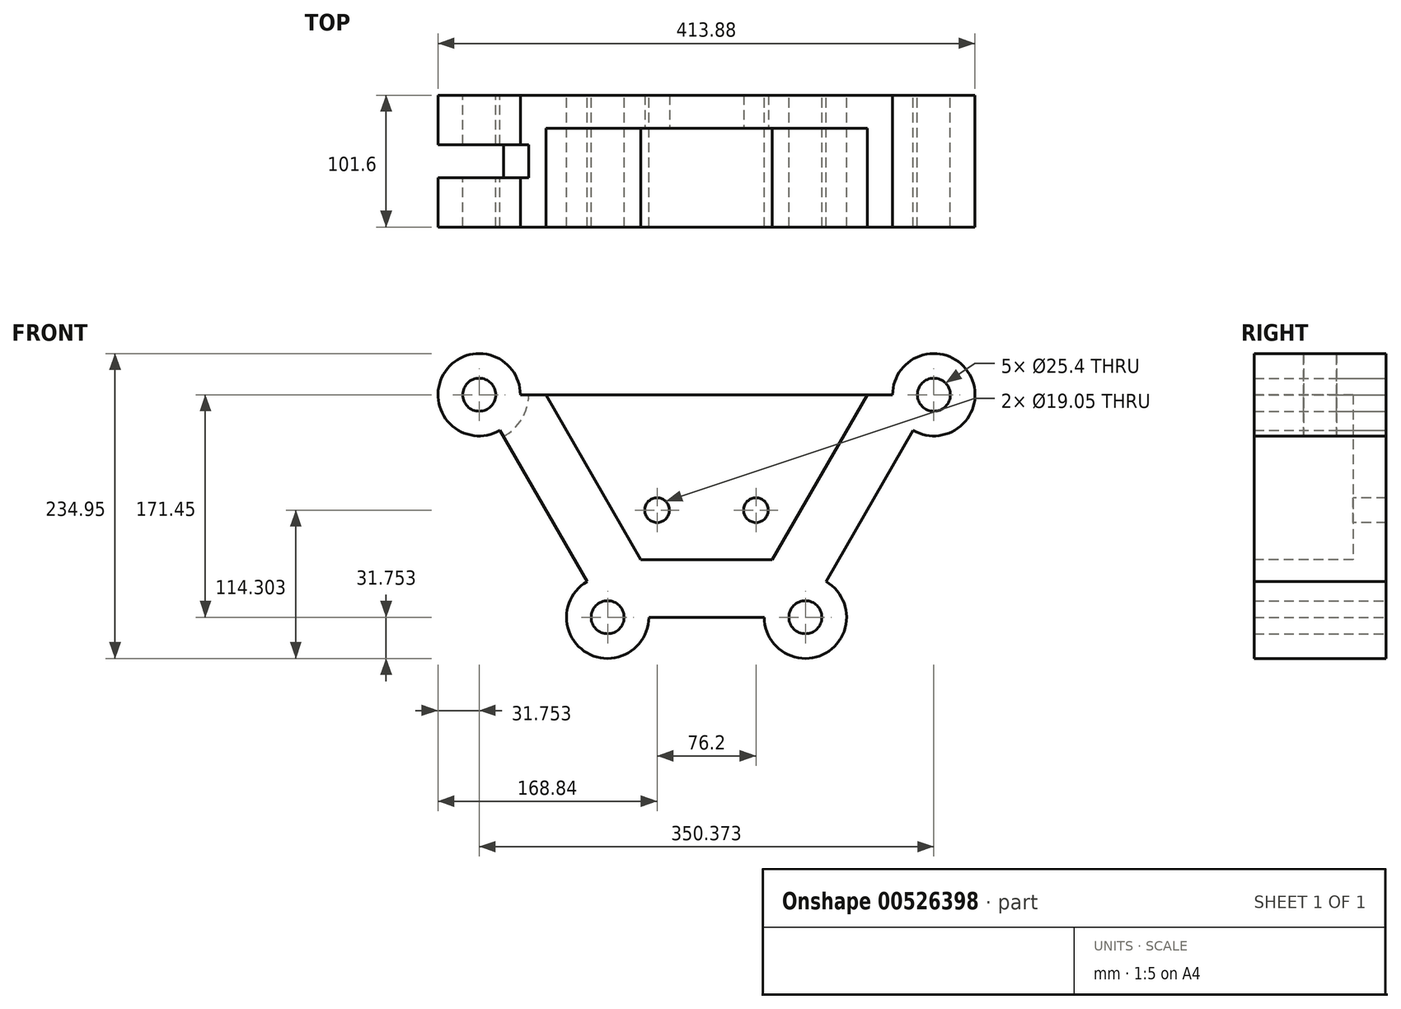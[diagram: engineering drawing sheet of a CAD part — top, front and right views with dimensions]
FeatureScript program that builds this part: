
annotation { "Feature Type Name" : "Feature", "Feature Type Description" : "" }
export const myFeature = defineFeature(function(context is Context, id is Id, definition is map)
    precondition{}
    {
        {
            var Q0;
            Q0=qCreatedBy(makeId("Front.planeOp"),FACE);
            var sketch = newSketch(context, id + "F0", { "sketchPlane" : qUnion([Q0])});
            skLineSegment(sketch, "E0", {"start": v(-76.2, -88.68) * mm, "end": v(76.2, -88.68) * mm});
            skLineSegment(sketch, "E1", {"start": v(-175.19, 82.77) * mm, "end": v(175.19, 82.77) * mm});
            skLineSegment(sketch, "E2", {"start": v(0, 82.77) * mm, "end": v(0, -88.68) * mm, "construction": true});
            skLineSegment(sketch, "E3", {"start": v(175.19, 82.77) * mm, "end": v(76.2, -88.68) * mm});
            skLineSegment(sketch, "E4", {"start": v(-175.19, 82.77) * mm, "end": v(-76.2, -88.68) * mm});
            skCircle(sketch, "E5", {"center": v(-175.19, 82.77) * mm, "radius": 31.75 * mm});
            skCircle(sketch, "E6", {"center": v(-175.19, 82.77) * mm, "radius": 12.7 * mm});
            skCircle(sketch, "E7", {"center": v(175.19, 82.77) * mm, "radius": 12.7 * mm});
            skCircle(sketch, "E8", {"center": v(76.2, -88.68) * mm, "radius": 12.7 * mm});
            skCircle(sketch, "E9", {"center": v(-76.2, -88.68) * mm, "radius": 12.7 * mm});
            skCircle(sketch, "E10", {"center": v(175.19, 82.77) * mm, "radius": 31.75 * mm});
            skCircle(sketch, "E11", {"center": v(76.2, -88.68) * mm, "radius": 31.75 * mm});
            skCircle(sketch, "E12", {"center": v(-76.2, -88.68) * mm, "radius": 31.75 * mm});
            skSolve(sketch);
        }
        {
            var Q0;
            {var subQ3=sQuery(id+"F0.wireOp",EDGE,"E12");var subQ10=sQuery(id+"F0.wireOp",EDGE,"E0");var subQ11=makeQuery(id+"F0.imprint","INTERSECT",VERTEX,{"derivedFrom":[subQ10,subQ3]});Q0=makeQuery(id+"F0.imprint","IMPRINT",FACE,{"disambiguationData":[TD([[makeQuery(id+"F0.imprint","IMPRINT",EDGE,{"disambiguationData":[TD([[subQ11,-1.0]])],"derivedFrom":subQ10}),1.0]])]});}
            var Q1;
            {var subQ0=sQuery(id+"F0.wireOp",EDGE,"E5");var subQ1=sQuery(id+"F0.wireOp",EDGE,"E1");var subQ2=makeQuery(id+"F0.imprint","INTERSECT",VERTEX,{"derivedFrom":[subQ1,subQ0]});Q1=makeQuery(id+"F0.imprint","IMPRINT",FACE,{"disambiguationData":[TD([[makeQuery(id+"F0.imprint","IMPRINT",EDGE,{"disambiguationData":[TD([[subQ2,1.0]])],"derivedFrom":subQ1}),-1.0]])]});}
            var Q2;
            {var subQ0=sQuery(id+"F0.wireOp",EDGE,"E5");var subQ1=sQuery(id+"F0.wireOp",EDGE,"E1");var subQ2=makeQuery(id+"F0.imprint","INTERSECT",VERTEX,{"derivedFrom":[subQ1,subQ0]});Q2=makeQuery(id+"F0.imprint","IMPRINT",FACE,{"disambiguationData":[TD([[makeQuery(id+"F0.imprint","IMPRINT",EDGE,{"disambiguationData":[TD([[subQ2,1.0]])],"derivedFrom":subQ1}),1.0]])]});}
            var Q3;
            {var subQ0=sQuery(id+"F0.wireOp",EDGE,"E10");var subQ1=sQuery(id+"F0.wireOp",EDGE,"E1");var subQ2=makeQuery(id+"F0.imprint","INTERSECT",VERTEX,{"derivedFrom":[subQ1,subQ0]});Q3=makeQuery(id+"F0.imprint","IMPRINT",FACE,{"disambiguationData":[TD([[makeQuery(id+"F0.imprint","IMPRINT",EDGE,{"disambiguationData":[TD([[subQ2,-1.0]])],"derivedFrom":subQ1}),1.0]])]});}
            var Q4;
            {var subQ0=sQuery(id+"F0.wireOp",EDGE,"E10");var subQ1=sQuery(id+"F0.wireOp",EDGE,"E1");var subQ2=makeQuery(id+"F0.imprint","INTERSECT",VERTEX,{"derivedFrom":[subQ1,subQ0]});Q4=makeQuery(id+"F0.imprint","IMPRINT",FACE,{"disambiguationData":[TD([[makeQuery(id+"F0.imprint","IMPRINT",EDGE,{"disambiguationData":[TD([[subQ2,-1.0]])],"derivedFrom":subQ1}),-1.0]])]});}
            var Q5;
            {var subQ0=sQuery(id+"F0.wireOp",EDGE,"E11");var subQ1=sQuery(id+"F0.wireOp",EDGE,"E0");var subQ2=makeQuery(id+"F0.imprint","INTERSECT",VERTEX,{"derivedFrom":[subQ1,subQ0]});Q5=makeQuery(id+"F0.imprint","IMPRINT",FACE,{"disambiguationData":[TD([[makeQuery(id+"F0.imprint","IMPRINT",EDGE,{"disambiguationData":[TD([[subQ2,-1.0]])],"derivedFrom":subQ1}),-1.0]])]});}
            var Q6;
            {var subQ0=sQuery(id+"F0.wireOp",EDGE,"E11");var subQ1=sQuery(id+"F0.wireOp",EDGE,"E0");var subQ2=makeQuery(id+"F0.imprint","INTERSECT",VERTEX,{"derivedFrom":[subQ1,subQ0]});Q6=makeQuery(id+"F0.imprint","IMPRINT",FACE,{"disambiguationData":[TD([[makeQuery(id+"F0.imprint","IMPRINT",EDGE,{"disambiguationData":[TD([[subQ2,-1.0]])],"derivedFrom":subQ1}),1.0]])]});}
            var Q7;
            {var subQ0=sQuery(id+"F0.wireOp",EDGE,"E12");var subQ1=sQuery(id+"F0.wireOp",EDGE,"E0");var subQ2=makeQuery(id+"F0.imprint","INTERSECT",VERTEX,{"derivedFrom":[subQ1,subQ0]});Q7=makeQuery(id+"F0.imprint","IMPRINT",FACE,{"disambiguationData":[TD([[makeQuery(id+"F0.imprint","IMPRINT",EDGE,{"disambiguationData":[TD([[subQ2,1.0]])],"derivedFrom":subQ1}),-1.0]])]});}
            var Q8;
            {var subQ0=sQuery(id+"F0.wireOp",EDGE,"E12");var subQ1=sQuery(id+"F0.wireOp",EDGE,"E0");var subQ2=makeQuery(id+"F0.imprint","INTERSECT",VERTEX,{"derivedFrom":[subQ1,subQ0]});Q8=makeQuery(id+"F0.imprint","IMPRINT",FACE,{"disambiguationData":[TD([[makeQuery(id+"F0.imprint","IMPRINT",EDGE,{"disambiguationData":[TD([[subQ2,1.0]])],"derivedFrom":subQ1}),1.0]])]});}
            extrude(context, id + "F1", {"entities" : qUnion([Q0, Q1, Q2, Q3, Q4, Q5, Q6, Q7, Q8]), "endBound" : BoundingType.SYMMETRIC, "depth" : 101.6 * mm, "offsetDistance" : 25.4 * mm});
        }
        {
            var Q0;
            Q0=makeQuery(id+"F1.opExtrude","CAP_FACE",FACE,{"disambiguationData":[OSD([sQuery(id+"F0.wireOp",EDGE,"E0"),sQuery(id+"F0.wireOp",EDGE,"E1"),sQuery(id+"F0.wireOp",EDGE,"E3"),sQuery(id+"F0.wireOp",EDGE,"E4"),sQuery(id+"F0.wireOp",EDGE,"E5"),sQuery(id+"F0.wireOp",EDGE,"E6"),sQuery(id+"F0.wireOp",EDGE,"E7"),sQuery(id+"F0.wireOp",EDGE,"E8"),sQuery(id+"F0.wireOp",EDGE,"E9"),sQuery(id+"F0.wireOp",EDGE,"E10"),sQuery(id+"F0.wireOp",EDGE,"E11"),sQuery(id+"F0.wireOp",EDGE,"E12")])],"isStart":false});
            var sketch = newSketch(context, id + "F2", { "sketchPlane" : qUnion([Q0])});
            skLineSegment(sketch, "E13.0", {"start": v(123.86, 82.77) * mm, "end": v(50.54, -44.23) * mm});
            skLineSegment(sketch, "E13.1", {"start": v(-50.54, -44.23) * mm, "end": v(50.54, -44.23) * mm});
            skLineSegment(sketch, "E13.2", {"start": v(-123.86, 82.77) * mm, "end": v(-50.54, -44.23) * mm});
            skLineSegment(sketch, "E14", {"start": v(-123.86, 82.77) * mm, "end": v(123.86, 82.77) * mm});
            skSolve(sketch);
        }
        {
            var Q0;
            Q0=makeQuery(id+"F2.imprint","IMPRINT",FACE,{"disambiguationData":[TD([[makeQuery(id+"F2.imprint","IMPRINT",EDGE,{"derivedFrom":sQuery(id+"F2.wireOp",EDGE,"E13.0")}),-1.0]])]});
            extrude(context, id + "F3", {"entities" : qUnion([Q0]), "operationType" : NewBodyOperationType.REMOVE, "oppositeDirection" : true, "depth" : 76.2 * mm, "offsetDistance" : 25.4 * mm});
        }
        {
            var Q0;
            Q0=qCreatedBy(makeId("Front.planeOp"),FACE);
            var sketch = newSketch(context, id + "F4", { "sketchPlane" : qUnion([Q0])});
            skCircle(sketch, "E15", {"center": v(-175, 83.77) * mm, "radius": 38.1 * mm});
            skCircle(sketch, "E16", {"center": v(175.86, 82.17) * mm, "radius": 38.1 * mm});
            skCircle(sketch, "E17", {"center": v(77.16, -88.7) * mm, "radius": 38.1 * mm});
            skCircle(sketch, "E18", {"center": v(-75.55, -87.77) * mm, "radius": 38.1 * mm});
            skSolve(sketch);
        }
        {
            var Q0;
            Q0=makeQuery(id+"F4.imprint","IMPRINT",FACE,{"disambiguationData":[TD([[makeQuery(id+"F4.imprint","IMPRINT",EDGE,{"derivedFrom":sQuery(id+"F4.wireOp",EDGE,"E15")}),1.0]])]});
            extrude(context, id + "F5", {"entities" : qUnion([Q0]), "operationType" : NewBodyOperationType.REMOVE, "endBound" : BoundingType.SYMMETRIC, "oppositeDirection" : true, "depth" : 25.4 * mm, "offsetDistance" : 25.4 * mm});
        }
        {
            var Q0;
            Q0=makeQuery(id+"F3.boolean.opBoolean","COPY",FACE,{"derivedFrom":makeQuery(id+"F3.opExtrude","CAP_FACE",FACE,{"disambiguationData":[OSD([sQuery(id+"F2.wireOp",EDGE,"E13.0"),sQuery(id+"F2.wireOp",EDGE,"E13.1"),sQuery(id+"F2.wireOp",EDGE,"E13.2"),sQuery(id+"F2.wireOp",EDGE,"E14")])],"isStart":false})});
            var sketch = newSketch(context, id + "F6", { "sketchPlane" : qUnion([Q0])});
            skLineSegment(sketch, "E19", {"start": v(0, -44.23) * mm, "end": v(0, -6.13) * mm, "construction": true});
            skLineSegment(sketch, "E20", {"start": v(-38.1, -6.13) * mm, "end": v(38.1, -6.13) * mm, "construction": true});
            skCircle(sketch, "E21", {"center": v(-38.1, -6.13) * mm, "radius": 9.53 * mm});
            skCircle(sketch, "E22", {"center": v(38.1, -6.13) * mm, "radius": 9.53 * mm});
            skSolve(sketch);
        }
        {
            var Q0;
            Q0=makeQuery(id+"F6.imprint","IMPRINT",FACE,{"disambiguationData":[TD([[makeQuery(id+"F6.imprint","IMPRINT",EDGE,{"derivedFrom":sQuery(id+"F6.wireOp",EDGE,"E21")}),1.0]])]});
            var Q1;
            Q1=makeQuery(id+"F6.imprint","IMPRINT",FACE,{"disambiguationData":[TD([[makeQuery(id+"F6.imprint","IMPRINT",EDGE,{"derivedFrom":sQuery(id+"F6.wireOp",EDGE,"E22")}),1.0]])]});
            extrude(context, id + "F7", {"entities" : qUnion([Q0, Q1]), "operationType" : NewBodyOperationType.REMOVE, "endBound" : BoundingType.THROUGH_ALL, "oppositeDirection" : true, "depth" : 25.4 * mm, "offsetDistance" : 25.4 * mm});
        }
    });
